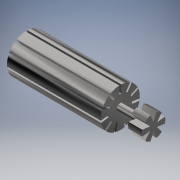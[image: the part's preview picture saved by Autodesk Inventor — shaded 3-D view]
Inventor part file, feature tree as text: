
AUTODESK INVENTOR PART (.ipt)
format: ipt  version: 2018 (Build 220112000, 112)  size: 209,408 bytes
history: native  units: in
note: dims shown in document units (in); Inventor stores cm internally (conversion verified against a paired STEP export)
features: sketch x3, extrude x2, revolve x1
ambient origin geometry x8: Origin, YZ Plane, XZ Plane, XY Plane, X Axis, Y Axis, Z Axis, Center Point
bodies: Solid1 (feature_tree)
feature tree (6):
  extrude  "Extrusion1"  Depth=10.0in
  revolve  "Revolution1"  [1 undecoded]
  extrude  "Extrusion2"  Depth=48.0in
  sketch  "Sketch1"  dims[d0=4.3307in d2=360.0deg d4=10.0in]
  sketch  "Sketch2"  dims[d5=6.0in d6=1.0in]
  sketch  "Sketch3"  dims[d7=48.0in d8=0.0in d9=4.0in d10=7.0in d11=12.0in d12=10.0in d13=90.0deg d14=2.0in d15=45.0deg d16=2.3622in d18=360.0deg d20=48.0in d21=0.0in]
note: 1 required parameter value undecoded (feature->parameter linkage not recoverable at this tier; creation-order binding heuristic only, values carry confidence <= 0.55)
